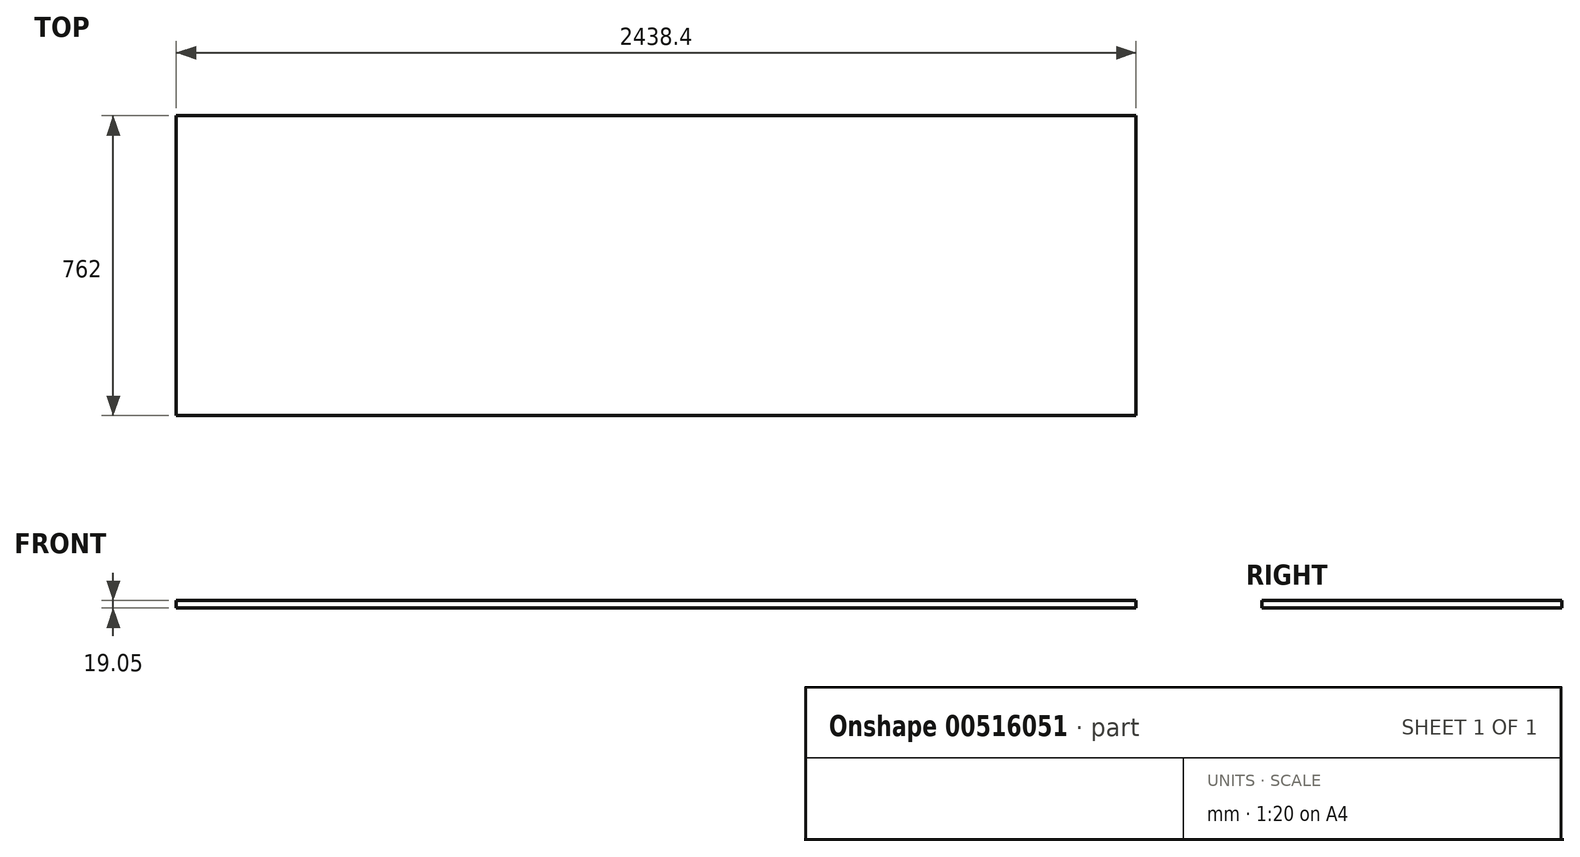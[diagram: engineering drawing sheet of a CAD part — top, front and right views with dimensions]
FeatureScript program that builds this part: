
annotation { "Feature Type Name" : "Feature", "Feature Type Description" : "" }
export const myFeature = defineFeature(function(context is Context, id is Id, definition is map)
    precondition{}
    {
        {
            var Q0;
            Q0=qCreatedBy(makeId("Top.planeOp"),FACE);
            var sketch = newSketch(context, id + "F0", { "sketchPlane" : qUnion([Q0])});
            skLineSegment(sketch, "E0.bottom", {"start": v(1219.2, -381) * mm, "end": v(-1219.2, -381) * mm});
            skLineSegment(sketch, "E0.top", {"start": v(1219.2, 381) * mm, "end": v(-1219.2, 381) * mm});
            skLineSegment(sketch, "E0.left", {"start": v(1219.2, -381) * mm, "end": v(1219.2, 381) * mm});
            skLineSegment(sketch, "E0.right", {"start": v(-1219.2, -381) * mm, "end": v(-1219.2, 381) * mm});
            skPoint(sketch, "E0.middle", {"position": v(0, 0) * mm});
            skSolve(sketch);
        }
        {
            var Q0;
            Q0=makeQuery(id+"F0.imprint","IMPRINT",FACE,{"disambiguationData":[TD([[makeQuery(id+"F0.imprint","IMPRINT",EDGE,{"derivedFrom":sQuery(id+"F0.wireOp",EDGE,"E0.bottom")}),-1.0]])]});
            extrude(context, id + "F1", {"entities" : qUnion([Q0]), "depth" : 19.05 * mm, "offsetDistance" : 25.4 * mm});
        }
    });
